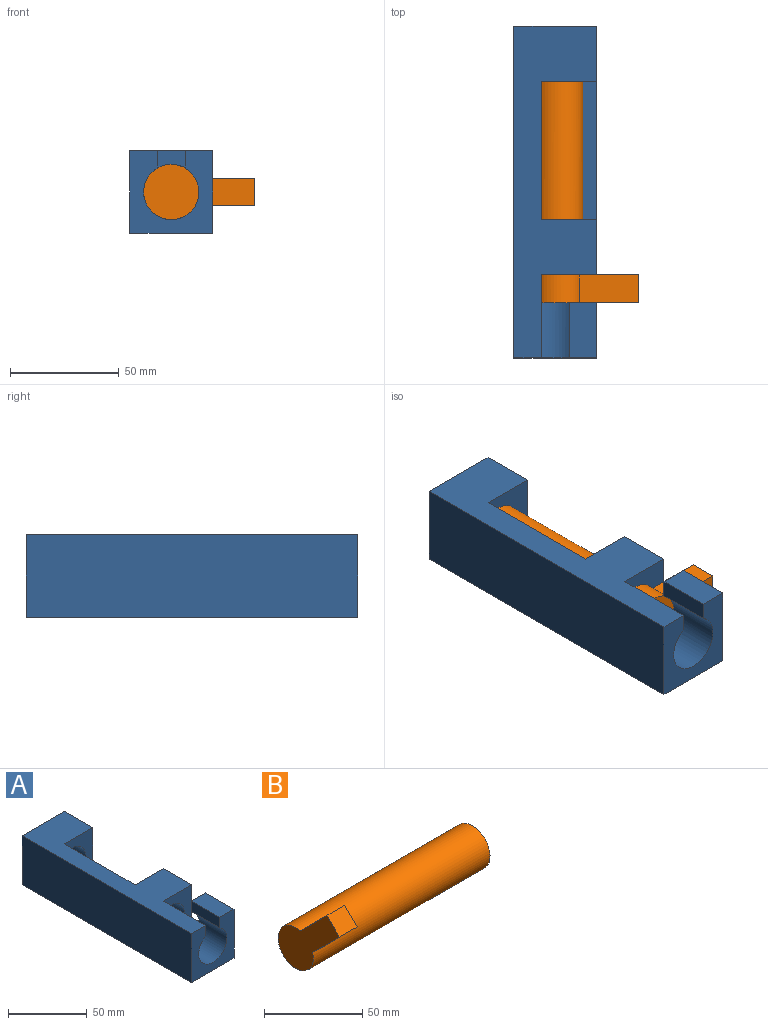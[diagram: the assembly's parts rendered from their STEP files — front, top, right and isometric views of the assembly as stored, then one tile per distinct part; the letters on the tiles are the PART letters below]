
ASSEMBLY  parts=2 mates=1
PART A: 17 faces, bbox 38.1x152.4x38.1 mm
  f0: plane 152.4x38.1mm, normal (1,0,0), area 3871mm2, adj f1,f2,f3,f4,f5,f7,f8,f9
  f1: plane 152.4x38.1mm, normal (0,0,1), area 3225.8mm2, adj f0,f2,f4,f6,f9,f10,f13,f14
  f2: plane 38.1x38.1mm, normal (0,-1,0), area 857.3mm2, adj f0,f1,f3,f5,f6,f10,f11,f12
  f3: plane 152.4x38.1mm, normal (0,0,-1), area 5806.4mm2, adj f0,f2,f4,f6
  f4: plane 38.1x38.1mm, normal (0,1,0), area 944.9mm2, adj f0,f1,f3,f6,f12
  f5: plane 25.4x12.7mm, normal (0,0,1), area 322.6mm2, adj f0,f2,f7,f11
  f6: plane 152.4x38.1mm, normal (-1,0,0), area 5806.4mm2, adj f1,f2,f3,f4
  f7: plane 25.4x12.7mm, normal (0,1,0), area 236.2mm2, adj f0,f5,f8,f11,f12
  f8: plane 12.7x8.05mm, normal (0,0,1), area 102.3mm2, adj f0,f7,f9,f12
  f9: plane 25.4x25.4mm, normal (0,-1,0), area 323.9mm2, adj f0,f1,f8,f10,f12
  f10: plane 38.1x8.05mm, normal (1,0,0), area 306.8mm2, adj f1,f2,f9,f12
  f11: plane 25.4x8.05mm, normal (-1,0,0), area 204.5mm2, adj f2,f5,f7,f12
  f12: cylinder r=12.7mm len=152.4mm, axis (0,1,0), area 9289.6mm2, adj f2,f4,f7,f8,f9,f10,f11,f13
  f13: plane 25.4x25.4mm, normal (0,-1,0), area 323.9mm2, adj f0,f1,f12,f15,f16
  f14: plane 25.4x25.4mm, normal (0,1,0), area 323.9mm2, adj f0,f1,f12,f15,f16
  f15: plane 63.5x8.05mm, normal (0,0,1), area 511.3mm2, adj f0,f12,f13,f14
  f16: plane 63.5x8.05mm, normal (1,0,0), area 511.3mm2, adj f1,f12,f13,f14
PART B: 7 faces, bbox 127x44.1x44.1 mm
  f0: cylinder r=12.7mm len=127mm, axis (1,0,0), area 9965.2mm2, adj f1,f2,f3,f5,f6
  f1: plane 44.13x44.13mm, normal (-1,0,0), area 836.3mm2, adj f0,f2,f3,f4
  f2: plane 19.16x19.16mm, normal (0,0.71,0.71), area 344.2mm2, adj f0,f1,f4,f5
  f3: plane 19.16x19.16mm, normal (0,-0.71,-0.71), area 344.2mm2, adj f0,f1,f4,f5
  f4: plane 12.7x8.98mm, normal (0,-0.71,0.71), area 161.3mm2, adj f1,f2,f3,f5
  f5: plane 28.14x28.14mm, normal (1,0,0), area 329.6mm2, adj f0,f2,f3,f4
  f6: plane 25.4x25.4mm, normal (1,0,0), area 506.7mm2, adj f0
PLACE A t=(-44.92,-84.12,24.47)mm fixed
PLACE B rot(axis=(0.36,0.36,0.86),98.4deg) t=(-63.97,55.58,43.52)mm
MATE cylindrical B.f0 <-> A.f12  axis (0,1,0) through (-63.97,68.28,43.52)mm
